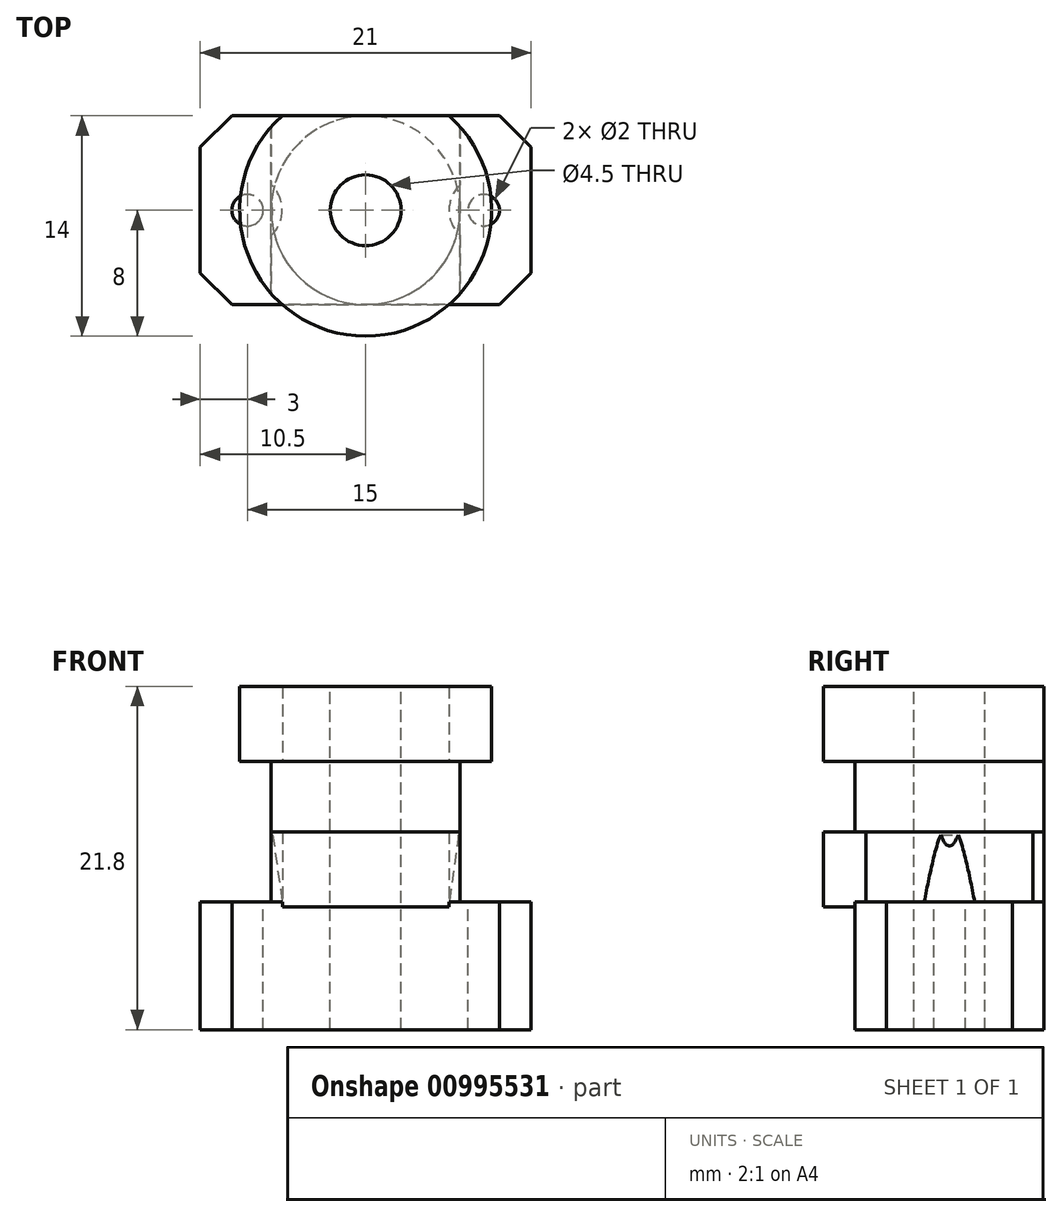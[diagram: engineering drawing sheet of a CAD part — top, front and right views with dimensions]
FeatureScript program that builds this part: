
annotation { "Feature Type Name" : "Feature", "Feature Type Description" : "" }
export const myFeature = defineFeature(function(context is Context, id is Id, definition is map)
    precondition{}
    {
        {
            var Q0;
            Q0=qCreatedBy(makeId("Front.planeOp"),FACE);
            var sketch = newSketch(context, id + "F0", { "sketchPlane" : qUnion([Q0])});
            skLineSegment(sketch, "E0", {"start": v(0, 0) * mm, "end": v(0, -14) * mm});
            skLineSegment(sketch, "E1", {"start": v(0, -14) * mm, "end": v(8, -14) * mm});
            skLineSegment(sketch, "E2", {"start": v(8, -14) * mm, "end": v(8, -9.25) * mm});
            skLineSegment(sketch, "E3", {"start": v(8, -9.25) * mm, "end": v(6, -9.25) * mm});
            skLineSegment(sketch, "E4", {"start": v(6, -9.25) * mm, "end": v(6, -4.75) * mm});
            skLineSegment(sketch, "E5", {"start": v(6, -4.75) * mm, "end": v(8, -4.75) * mm});
            skLineSegment(sketch, "E6", {"start": v(8, -4.75) * mm, "end": v(8, 0) * mm});
            skLineSegment(sketch, "E7", {"start": v(8, 0) * mm, "end": v(0, 0) * mm});
            skLineSegment(sketch, "E8", {"start": v(6, -9.25) * mm, "end": v(0, -9.25) * mm});
            skSolve(sketch);
        }
        {
            var Q0;
            Q0=makeQuery(id+"F0.imprint","IMPRINT",FACE,{"disambiguationData":[TD([[makeQuery(id+"F0.imprint","IMPRINT",EDGE,{"derivedFrom":sQuery(id+"F0.wireOp",EDGE,"E4")}),1.0]])]});
            var Q1;
            {var subQ0=sQuery(id+"F0.wireOp",EDGE,"E1");Q1=makeQuery(id+"F0.imprint","IMPRINT",FACE,{"disambiguationData":[TD([[makeQuery(id+"F0.imprint","IMPRINT",EDGE,{"derivedFrom":subQ0}),1.0]])]});}
            var Q2;
            Q2=sQuery(id+"F0.wireOp",EDGE,"E0");
            revolve(context, id + "F1", {"surfaceOperationType" : NewSurfaceOperationType.NEW, "entities" : qUnion([Q0, Q1]), "axis" : qUnion([Q2]), "revolveType" : RevolveType.FULL});
        }
        {
            var Q0;
            Q0=makeQuery(id+"F1.opRevolve","SWEPT_FACE",FACE,{"disambiguationData":[OSD([sQuery(id+"F0.wireOp",EDGE,"E7")])]});
            var sketch = newSketch(context, id + "F2", { "sketchPlane" : qUnion([Q0])});
            skCircle(sketch, "E9", {"center": v(0, 0) * mm, "radius": 2.25 * mm});
            skSolve(sketch);
        }
        {
            var Q0;
            Q0 = qSketchRegion(id + "F2", true);
            extrude(context, id + "F3", {"entities" : qUnion([Q0]), "operationType" : NewBodyOperationType.REMOVE, "endBound" : BoundingType.THROUGH_ALL, "oppositeDirection" : true, "depth" : 25 * mm, "offsetDistance" : 25 * mm});
        }
        {
            var Q0;
            Q0=makeQuery(id+"F1.opRevolve","SWEPT_FACE",FACE,{"disambiguationData":[OSD([sQuery(id+"F0.wireOp",EDGE,"E7")])]});
            cPlane(context, id + "F4", {"entities" : qUnion([Q0]), "cplaneType" : CPlaneType.OFFSET, "offset" : (23.6 - 1.8) * mm, "oppositeDirection" : true, "width" : 150 * mm, "height" : 150 * mm});
        }
        {
            var Q0;
            Q0=qCreatedBy(id+"F4.planeOp",FACE);
            var sketch = newSketch(context, id + "F5", { "sketchPlane" : qUnion([Q0])});
            skLineSegment(sketch, "E10.bottom", {"start": v(10.5, 6) * mm, "end": v(-10.5, 6) * mm});
            skLineSegment(sketch, "E10.top", {"start": v(10.5, -6) * mm, "end": v(-10.5, -6) * mm});
            skLineSegment(sketch, "E10.left", {"start": v(10.5, 6) * mm, "end": v(10.5, -6) * mm});
            skLineSegment(sketch, "E10.right", {"start": v(-10.5, 6) * mm, "end": v(-10.5, -6) * mm});
            skPoint(sketch, "E10.middle", {"position": v(0, 0) * mm});
            skSolve(sketch);
        }
        {
            var Q0;
            Q0=makeQuery(id+"F5.imprint","IMPRINT",FACE,{"disambiguationData":[TD([[makeQuery(id+"F5.imprint","IMPRINT",EDGE,{"derivedFrom":sQuery(id+"F5.wireOp",EDGE,"E10.bottom")}),1.0]])]});
            extrude(context, id + "F6", {"entities" : qUnion([Q0]), "operationType" : NewBodyOperationType.ADD, "depth" : 8.1 * mm, "offsetDistance" : 25 * mm});
        }
        {
            var Q0;
            Q0=makeQuery(id+"F6.opExtrude","CAP_FACE",FACE,{"disambiguationData":[OSD([sQuery(id+"F5.wireOp",EDGE,"E10.bottom"),sQuery(id+"F5.wireOp",EDGE,"E10.top"),sQuery(id+"F5.wireOp",EDGE,"E10.left"),sQuery(id+"F5.wireOp",EDGE,"E10.right")])],"isStart":false});
            var sketch = newSketch(context, id + "F7", { "sketchPlane" : qUnion([Q0])});
            skPoint(sketch, "E11", {"position": v(-7.5, 0) * mm});
            skPoint(sketch, "E12", {"position": v(7.5, 0) * mm});
            skCircle(sketch, "E13", {"center": v(-7.5, 0) * mm, "radius": 1 * mm});
            skCircle(sketch, "E14", {"center": v(7.5, 0) * mm, "radius": 1 * mm});
            skCircle(sketch, "E15", {"center": v(7.5, 0) * mm, "radius": 2.2 * mm});
            skCircle(sketch, "E16", {"center": v(-7.5, 0) * mm, "radius": 2.2 * mm});
            skSolve(sketch);
        }
        {
            var Q0;
            {var subQ0=sQuery(id+"F7.wireOp",EDGE,"E13");var subQ1=makeQuery(id+"F6.boolean.opBoolean","INTERSECT",EDGE,{"disambiguationData":[OD(1.0)],"derivedFrom":[makeQuery(id+"F1.opRevolve","SWEPT_FACE",FACE,{"disambiguationData":[OSD([sQuery(id+"F0.wireOp",EDGE,"E2")])]}),makeQuery(id+"F6.opExtrude","CAP_FACE",FACE,{"disambiguationData":[OSD([sQuery(id+"F5.wireOp",EDGE,"E10.bottom"),sQuery(id+"F5.wireOp",EDGE,"E10.top"),sQuery(id+"F5.wireOp",EDGE,"E10.left"),sQuery(id+"F5.wireOp",EDGE,"E10.right")])],"isStart":false})]});var subQ2=makeQuery(id+"F7.imprint","INTERSECT",VERTEX,{"disambiguationData":[OD(0.0)],"derivedFrom":[subQ1,subQ0]});Q0=makeQuery(id+"F7.imprint","IMPRINT",FACE,{"disambiguationData":[TD([[makeQuery(id+"F7.imprint","IMPRINT",EDGE,{"disambiguationData":[TD([[subQ2,1.0]])],"derivedFrom":subQ0}),1.0]])]});}
            var Q1;
            {var subQ0=sQuery(id+"F7.wireOp",EDGE,"E13");var subQ1=makeQuery(id+"F6.boolean.opBoolean","INTERSECT",EDGE,{"disambiguationData":[OD(1.0)],"derivedFrom":[makeQuery(id+"F1.opRevolve","SWEPT_FACE",FACE,{"disambiguationData":[OSD([sQuery(id+"F0.wireOp",EDGE,"E2")])]}),makeQuery(id+"F6.opExtrude","CAP_FACE",FACE,{"disambiguationData":[OSD([sQuery(id+"F5.wireOp",EDGE,"E10.bottom"),sQuery(id+"F5.wireOp",EDGE,"E10.top"),sQuery(id+"F5.wireOp",EDGE,"E10.left"),sQuery(id+"F5.wireOp",EDGE,"E10.right")])],"isStart":false})]});var subQ2=makeQuery(id+"F7.imprint","INTERSECT",VERTEX,{"disambiguationData":[OD(0.0)],"derivedFrom":[subQ1,subQ0]});Q1=makeQuery(id+"F7.imprint","IMPRINT",FACE,{"disambiguationData":[TD([[makeQuery(id+"F7.imprint","IMPRINT",EDGE,{"disambiguationData":[TD([[subQ2,-1.0]])],"derivedFrom":subQ0}),1.0]])]});}
            var Q2;
            {var subQ0=sQuery(id+"F7.wireOp",EDGE,"E14");var subQ1=makeQuery(id+"F6.boolean.opBoolean","INTERSECT",EDGE,{"disambiguationData":[OD(0.0)],"derivedFrom":[makeQuery(id+"F1.opRevolve","SWEPT_FACE",FACE,{"disambiguationData":[OSD([sQuery(id+"F0.wireOp",EDGE,"E2")])]}),makeQuery(id+"F6.opExtrude","CAP_FACE",FACE,{"disambiguationData":[OSD([sQuery(id+"F5.wireOp",EDGE,"E10.bottom"),sQuery(id+"F5.wireOp",EDGE,"E10.top"),sQuery(id+"F5.wireOp",EDGE,"E10.left"),sQuery(id+"F5.wireOp",EDGE,"E10.right")])],"isStart":false})]});var subQ2=makeQuery(id+"F7.imprint","INTERSECT",VERTEX,{"disambiguationData":[OD(0.0)],"derivedFrom":[subQ1,subQ0]});Q2=makeQuery(id+"F7.imprint","IMPRINT",FACE,{"disambiguationData":[TD([[makeQuery(id+"F7.imprint","IMPRINT",EDGE,{"disambiguationData":[TD([[subQ2,1.0]])],"derivedFrom":subQ0}),1.0]])]});}
            var Q3;
            {var subQ0=sQuery(id+"F7.wireOp",EDGE,"E14");var subQ1=makeQuery(id+"F6.boolean.opBoolean","INTERSECT",EDGE,{"disambiguationData":[OD(0.0)],"derivedFrom":[makeQuery(id+"F1.opRevolve","SWEPT_FACE",FACE,{"disambiguationData":[OSD([sQuery(id+"F0.wireOp",EDGE,"E2")])]}),makeQuery(id+"F6.opExtrude","CAP_FACE",FACE,{"disambiguationData":[OSD([sQuery(id+"F5.wireOp",EDGE,"E10.bottom"),sQuery(id+"F5.wireOp",EDGE,"E10.top"),sQuery(id+"F5.wireOp",EDGE,"E10.left"),sQuery(id+"F5.wireOp",EDGE,"E10.right")])],"isStart":false})]});var subQ2=makeQuery(id+"F7.imprint","INTERSECT",VERTEX,{"disambiguationData":[OD(0.0)],"derivedFrom":[subQ1,subQ0]});Q3=makeQuery(id+"F7.imprint","IMPRINT",FACE,{"disambiguationData":[TD([[makeQuery(id+"F7.imprint","IMPRINT",EDGE,{"disambiguationData":[TD([[subQ2,-1.0]])],"derivedFrom":subQ0}),1.0]])]});}
            extrude(context, id + "F8", {"entities" : qUnion([Q0, Q1, Q2, Q3]), "operationType" : NewBodyOperationType.REMOVE, "endBound" : BoundingType.THROUGH_ALL, "oppositeDirection" : true, "depth" : 25 * mm, "offsetDistance" : 25 * mm});
        }
        {
            var Q0;
            Q0=makeQuery(id+"F1.opRevolve","SWEPT_FACE",FACE,{"disambiguationData":[OSD([sQuery(id+"F0.wireOp",EDGE,"E3")])]});
            var sketch = newSketch(context, id + "F9", { "sketchPlane" : qUnion([Q0])});
            skLineSegment(sketch, "E17.bottom", {"start": v(-6, -6) * mm, "end": v(6, -6) * mm});
            skLineSegment(sketch, "E17.top", {"start": v(-6, 6) * mm, "end": v(6, 6) * mm});
            skLineSegment(sketch, "E17.left", {"start": v(-6, -6) * mm, "end": v(-6, 6) * mm});
            skLineSegment(sketch, "E17.right", {"start": v(6, -6) * mm, "end": v(6, 6) * mm});
            skPoint(sketch, "E17.middle", {"position": v(0, 0) * mm});
            skLineSegment(sketch, "E18.bottom", {"start": v(-12.08, -9.75) * mm, "end": v(12.08, -9.75) * mm});
            skLineSegment(sketch, "E18.top", {"start": v(-12.08, 9.75) * mm, "end": v(12.08, 9.75) * mm});
            skLineSegment(sketch, "E18.left", {"start": v(-12.08, -9.75) * mm, "end": v(-12.08, 9.75) * mm});
            skLineSegment(sketch, "E18.right", {"start": v(12.08, -9.75) * mm, "end": v(12.08, 9.75) * mm});
            skSolve(sketch);
        }
        {
            var Q0;
            Q0=makeQuery(id+"F9.imprint","IMPRINT",FACE,{"disambiguationData":[TD([[makeQuery(id+"F9.imprint","IMPRINT",EDGE,{"derivedFrom":sQuery(id+"F9.wireOp",EDGE,"E18.bottom")}),1.0]])]});
            var Q1;
            {var subQ0=sQuery(id+"F9.wireOp",EDGE,"E17.right");var subQ1=sQuery(id+"F0.wireOp",EDGE,"E3");var subQ2=makeQuery(id+"F1.opRevolve","SWEPT_EDGE",EDGE,{"disambiguationData":[OSD([sQuery(id+"F0.wireOp",EDGE,"E2"),subQ1])]});var subQ3=makeQuery(id+"F9.imprint","INTERSECT",VERTEX,{"disambiguationData":[OD(0.0)],"derivedFrom":[subQ2,subQ0]});Q1=makeQuery(id+"F9.imprint","IMPRINT",FACE,{"disambiguationData":[TD([[makeQuery(id+"F9.imprint","IMPRINT",EDGE,{"disambiguationData":[TD([[subQ3,-1.0]])],"derivedFrom":subQ0}),-1.0]])]});}
            var Q2;
            {var subQ0=sQuery(id+"F9.wireOp",EDGE,"E17.left");var subQ1=sQuery(id+"F0.wireOp",EDGE,"E3");var subQ2=makeQuery(id+"F1.opRevolve","SWEPT_EDGE",EDGE,{"disambiguationData":[OSD([sQuery(id+"F0.wireOp",EDGE,"E2"),subQ1])]});var subQ3=makeQuery(id+"F9.imprint","INTERSECT",VERTEX,{"disambiguationData":[OD(0.0)],"derivedFrom":[subQ2,subQ0]});Q2=makeQuery(id+"F9.imprint","IMPRINT",FACE,{"disambiguationData":[TD([[makeQuery(id+"F9.imprint","IMPRINT",EDGE,{"disambiguationData":[TD([[subQ3,-1.0]])],"derivedFrom":subQ0}),1.0]])]});}
            var Q3;
            {var subQ0=sQuery(id+"F5.wireOp",EDGE,"E10.top");var subQ1=sQuery(id+"F5.wireOp",EDGE,"E10.bottom");var subQ2=sQuery(id+"F5.wireOp",EDGE,"E10.left");Q3=makeQuery(id+"F6.boolean.opBoolean","SPLIT",FACE,{"disambiguationData":[TD([makeQuery(id+"F6.opExtrude","SWEPT_FACE",FACE,{"disambiguationData":[OSD([subQ2])]})])],"derivedFrom":makeQuery(id+"F6.opExtrude","CAP_FACE",FACE,{"disambiguationData":[OSD([subQ1,subQ0,subQ2,sQuery(id+"F5.wireOp",EDGE,"E10.right")])],"isStart":false})});}
            extrude(context, id + "F10", {"entities" : qUnion([Q0, Q1, Q2]), "operationType" : NewBodyOperationType.REMOVE, "endBound" : BoundingType.UP_TO_SURFACE, "oppositeDirection" : true, "depth" : 25 * mm, "endBoundEntityFace" : qUnion([Q3]), "offsetDistance" : 25 * mm});
        }
        {
            var Q0;
            Q0=makeQuery(id+"F6.boolean.opBoolean","SPLIT",FACE,{"disambiguationData":[TD([makeQuery(id+"F6.opExtrude","SWEPT_FACE",FACE,{"disambiguationData":[OSD([sQuery(id+"F5.wireOp",EDGE,"E10.bottom")])]})])],"derivedFrom":makeQuery(id+"F1.opRevolve","SWEPT_FACE",FACE,{"disambiguationData":[OSD([sQuery(id+"F0.wireOp",EDGE,"E1")])]})});
            extrude(context, id + "F11", {"entities" : qUnion([Q0]), "operationType" : NewBodyOperationType.REMOVE, "endBound" : BoundingType.THROUGH_ALL, "oppositeDirection" : true, "depth" : 25 * mm, "offsetDistance" : 25 * mm});
        }
        {
            var Q0;
            Q0=makeQuery(id+"F6.boolean.opBoolean","SPLIT",FACE,{"disambiguationData":[TD([makeQuery(id+"F3.boolean.opBoolean","COPY",FACE,{"derivedFrom":makeQuery(id+"F3.opExtrude","SWEPT_FACE",FACE,{"disambiguationData":[OSD([sQuery(id+"F2.wireOp",EDGE,"E9")])]})})])],"derivedFrom":makeQuery(id+"F6.opExtrude","CAP_FACE",FACE,{"disambiguationData":[OSD([sQuery(id+"F5.wireOp",EDGE,"E10.bottom"),sQuery(id+"F5.wireOp",EDGE,"E10.top"),sQuery(id+"F5.wireOp",EDGE,"E10.left"),sQuery(id+"F5.wireOp",EDGE,"E10.right")])],"isStart":false})});
            extrude(context, id + "F12", {"entities" : qUnion([Q0]), "operationType" : NewBodyOperationType.REMOVE, "endBound" : BoundingType.THROUGH_ALL, "oppositeDirection" : true, "depth" : 25 * mm, "offsetDistance" : 25 * mm});
        }
        {
            var Q0;
            Q0=makeQuery(id+"F6.opExtrude","SWEPT_EDGE",EDGE,{"disambiguationData":[OSD([sQuery(id+"F5.wireOp",EDGE,"E10.top"),sQuery(id+"F5.wireOp",EDGE,"E10.left")])]});
            var Q1;
            Q1=makeQuery(id+"F6.opExtrude","SWEPT_EDGE",EDGE,{"disambiguationData":[OSD([sQuery(id+"F5.wireOp",EDGE,"E10.bottom"),sQuery(id+"F5.wireOp",EDGE,"E10.left")])]});
            var Q2;
            Q2=makeQuery(id+"F6.opExtrude","SWEPT_EDGE",EDGE,{"disambiguationData":[OSD([sQuery(id+"F5.wireOp",EDGE,"E10.bottom"),sQuery(id+"F5.wireOp",EDGE,"E10.right")])]});
            var Q3;
            Q3=makeQuery(id+"F6.opExtrude","SWEPT_EDGE",EDGE,{"disambiguationData":[OSD([sQuery(id+"F5.wireOp",EDGE,"E10.top"),sQuery(id+"F5.wireOp",EDGE,"E10.right")])]});
            chamfer(context, id + "F13", {"entities" : qUnion([Q0, Q1, Q2, Q3]), "width" : 2 * mm, "tangentPropagation" : true});
        }
        {
            var Q0;
            {var subQ0=sQuery(id+"F7.wireOp",EDGE,"E14");var subQ1=makeQuery(id+"F6.boolean.opBoolean","INTERSECT",EDGE,{"disambiguationData":[OD(0.0)],"derivedFrom":[makeQuery(id+"F1.opRevolve","SWEPT_FACE",FACE,{"disambiguationData":[OSD([sQuery(id+"F0.wireOp",EDGE,"E2")])]}),makeQuery(id+"F6.opExtrude","CAP_FACE",FACE,{"disambiguationData":[OSD([sQuery(id+"F5.wireOp",EDGE,"E10.bottom"),sQuery(id+"F5.wireOp",EDGE,"E10.top"),sQuery(id+"F5.wireOp",EDGE,"E10.left"),sQuery(id+"F5.wireOp",EDGE,"E10.right")])],"isStart":false})]});var subQ2=makeQuery(id+"F7.imprint","INTERSECT",VERTEX,{"disambiguationData":[OD(0.0)],"derivedFrom":[subQ1,subQ0]});Q0=makeQuery(id+"F7.imprint","IMPRINT",FACE,{"disambiguationData":[TD([[makeQuery(id+"F7.imprint","IMPRINT",EDGE,{"disambiguationData":[TD([[subQ2,-1.0]])],"derivedFrom":subQ0}),-1.0]])]});}
            var Q1;
            {var subQ0=sQuery(id+"F7.wireOp",EDGE,"E14");var subQ1=makeQuery(id+"F6.boolean.opBoolean","INTERSECT",EDGE,{"disambiguationData":[OD(0.0)],"derivedFrom":[makeQuery(id+"F1.opRevolve","SWEPT_FACE",FACE,{"disambiguationData":[OSD([sQuery(id+"F0.wireOp",EDGE,"E2")])]}),makeQuery(id+"F6.opExtrude","CAP_FACE",FACE,{"disambiguationData":[OSD([sQuery(id+"F5.wireOp",EDGE,"E10.bottom"),sQuery(id+"F5.wireOp",EDGE,"E10.top"),sQuery(id+"F5.wireOp",EDGE,"E10.left"),sQuery(id+"F5.wireOp",EDGE,"E10.right")])],"isStart":false})]});var subQ2=makeQuery(id+"F7.imprint","INTERSECT",VERTEX,{"disambiguationData":[OD(0.0)],"derivedFrom":[subQ1,subQ0]});Q1=makeQuery(id+"F7.imprint","IMPRINT",FACE,{"disambiguationData":[TD([[makeQuery(id+"F7.imprint","IMPRINT",EDGE,{"disambiguationData":[TD([[subQ2,1.0]])],"derivedFrom":subQ0}),-1.0]])]});}
            var Q2;
            {var subQ0=sQuery(id+"F7.wireOp",EDGE,"E13");var subQ1=makeQuery(id+"F6.boolean.opBoolean","INTERSECT",EDGE,{"disambiguationData":[OD(1.0)],"derivedFrom":[makeQuery(id+"F1.opRevolve","SWEPT_FACE",FACE,{"disambiguationData":[OSD([sQuery(id+"F0.wireOp",EDGE,"E2")])]}),makeQuery(id+"F6.opExtrude","CAP_FACE",FACE,{"disambiguationData":[OSD([sQuery(id+"F5.wireOp",EDGE,"E10.bottom"),sQuery(id+"F5.wireOp",EDGE,"E10.top"),sQuery(id+"F5.wireOp",EDGE,"E10.left"),sQuery(id+"F5.wireOp",EDGE,"E10.right")])],"isStart":false})]});var subQ2=makeQuery(id+"F7.imprint","INTERSECT",VERTEX,{"disambiguationData":[OD(0.0)],"derivedFrom":[subQ1,subQ0]});Q2=makeQuery(id+"F7.imprint","IMPRINT",FACE,{"disambiguationData":[TD([[makeQuery(id+"F7.imprint","IMPRINT",EDGE,{"disambiguationData":[TD([[subQ2,1.0]])],"derivedFrom":subQ0}),-1.0]])]});}
            var Q3;
            {var subQ0=sQuery(id+"F7.wireOp",EDGE,"E13");var subQ1=makeQuery(id+"F6.boolean.opBoolean","INTERSECT",EDGE,{"disambiguationData":[OD(1.0)],"derivedFrom":[makeQuery(id+"F1.opRevolve","SWEPT_FACE",FACE,{"disambiguationData":[OSD([sQuery(id+"F0.wireOp",EDGE,"E2")])]}),makeQuery(id+"F6.opExtrude","CAP_FACE",FACE,{"disambiguationData":[OSD([sQuery(id+"F5.wireOp",EDGE,"E10.bottom"),sQuery(id+"F5.wireOp",EDGE,"E10.top"),sQuery(id+"F5.wireOp",EDGE,"E10.left"),sQuery(id+"F5.wireOp",EDGE,"E10.right")])],"isStart":false})]});var subQ2=makeQuery(id+"F7.imprint","INTERSECT",VERTEX,{"disambiguationData":[OD(0.0)],"derivedFrom":[subQ1,subQ0]});Q3=makeQuery(id+"F7.imprint","IMPRINT",FACE,{"disambiguationData":[TD([[makeQuery(id+"F7.imprint","IMPRINT",EDGE,{"disambiguationData":[TD([[subQ2,-1.0]])],"derivedFrom":subQ0}),-1.0]])]});}
            var Q4;
            Q4=makeQuery(id+"F10.boolean.opBoolean","SPLIT",FACE,{"disambiguationData":[OD(1.0)],"derivedFrom":makeQuery(id+"F1.opRevolve","SWEPT_FACE",FACE,{"disambiguationData":[OSD([sQuery(id+"F0.wireOp",EDGE,"E3")])]})});
            extrude(context, id + "F14", {"entities" : qUnion([Q0, Q1, Q2, Q3]), "operationType" : NewBodyOperationType.REMOVE, "endBound" : BoundingType.UP_TO_SURFACE, "depth" : 25 * mm, "endBoundEntityFace" : qUnion([Q4]), "offsetDistance" : 25 * mm, "hasDraft" : true, "draftAngle" : 8 * degree, "draftPullDirection" : true});
        }
    });
